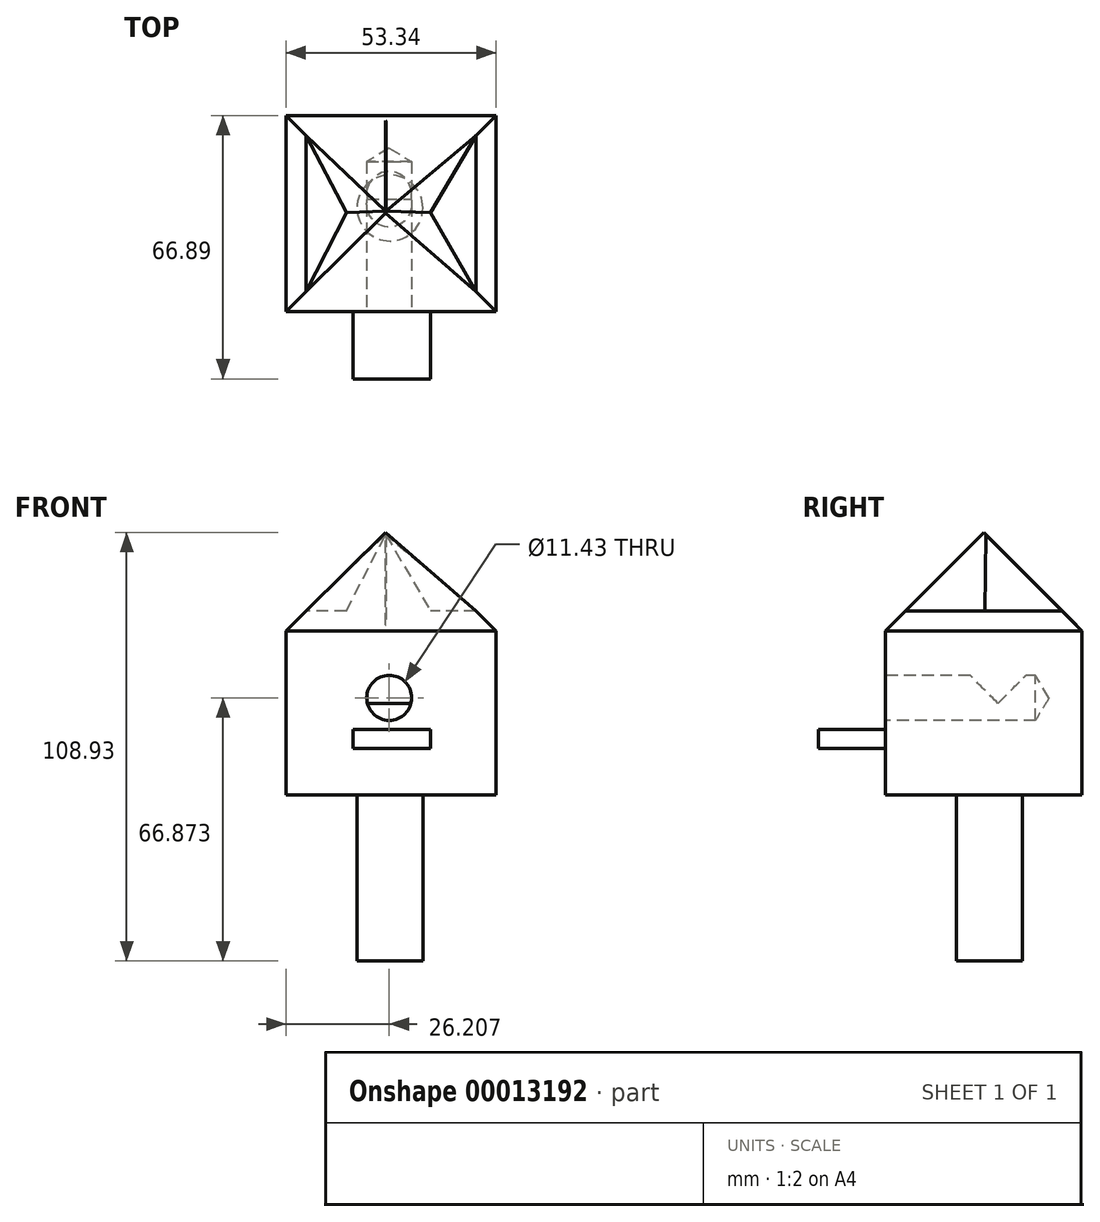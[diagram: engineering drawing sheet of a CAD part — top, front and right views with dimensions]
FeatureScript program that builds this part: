
annotation { "Feature Type Name" : "Feature", "Feature Type Description" : "" }
export const myFeature = defineFeature(function(context is Context, id is Id, definition is map)
    precondition{}
    {
        {
            var Q0;
            Q0=qCreatedBy(makeId("Front.planeOp"),FACE);
            var sketch = newSketch(context, id + "F0", { "sketchPlane" : qUnion([Q0])});
            skLineSegment(sketch, "E0.bottom", {"start": v(-41.12, 12.66) * mm, "end": v(12.22, 12.66) * mm});
            skLineSegment(sketch, "E0.top", {"start": v(-41.12, -34.12) * mm, "end": v(12.22, -34.12) * mm});
            skLineSegment(sketch, "E0.left", {"start": v(-41.12, 12.66) * mm, "end": v(-41.12, -34.12) * mm});
            skLineSegment(sketch, "E0.right", {"start": v(12.22, 12.66) * mm, "end": v(12.22, -34.12) * mm});
            skSolve(sketch);
        }
        {
            var Q0;
            Q0=makeQuery(id+"F0.imprint","IMPRINT",FACE,{"disambiguationData":[TD([[makeQuery(id+"F0.imprint","IMPRINT",EDGE,{"derivedFrom":sQuery(id+"F0.wireOp",EDGE,"E0.bottom")}),-1.0]])]});
            extrude(context, id + "F1", {"entities" : qUnion([Q0]), "oppositeDirection" : true, "depth" : 49.84 * mm});
        }
        {
            var Q0;
            Q0=makeQuery(id+"F1.opExtrude","SWEPT_FACE",FACE,{"disambiguationData":[OSD([sQuery(id+"F0.wireOp",EDGE,"E0.top")])]});
            var sketch = newSketch(context, id + "F2", { "sketchPlane" : qUnion([Q0])});
            skPoint(sketch, "E1", {"position": v(-14.75, -27.27) * mm});
            skSolve(sketch);
        }
        {
            var Q0;
            {var subQ0=sQuery(id+"F0.wireOp",EDGE,"E0.top");Q0=makeQuery(id+"F2.imprint","IMPRINT",FACE,{"disambiguationData":[TD([[makeQuery(id+"F2.imprint","IMPRINT",EDGE,{"derivedFrom":makeQuery(id+"F1.opExtrude","CAP_EDGE",EDGE,{"disambiguationData":[OSD([subQ0])],"isStart":true})}),-1.0]])]});}
            var sketch = newSketch(context, id + "F3", { "sketchPlane" : qUnion([Q0])});
            skCircle(sketch, "E2", {"center": v(-14.75, -26.37) * mm, "radius": 8.4 * mm});
            skSolve(sketch);
        }
        {
            var Q0;
            Q0=makeQuery(id+"F3.imprint","IMPRINT",FACE,{"disambiguationData":[TD([[makeQuery(id+"F3.imprint","IMPRINT",EDGE,{"derivedFrom":sQuery(id+"F3.wireOp",EDGE,"E2")}),1.0]])]});
            extrude(context, id + "F4", {"entities" : qUnion([Q0]), "operationType" : NewBodyOperationType.ADD, "depth" : 42.22 * mm});
        }
        {
            var Q0;
            Q0=makeQuery(id+"F1.opExtrude","CAP_FACE",FACE,{"disambiguationData":[OSD([sQuery(id+"F0.wireOp",EDGE,"E0.bottom"),sQuery(id+"F0.wireOp",EDGE,"E0.top"),sQuery(id+"F0.wireOp",EDGE,"E0.left"),sQuery(id+"F0.wireOp",EDGE,"E0.right")])],"isStart":true});
            var sketch = newSketch(context, id + "F5", { "sketchPlane" : qUnion([Q0])});
            skPoint(sketch, "E3", {"position": v(-14.91, -9.47) * mm});
            skSolve(sketch);
        }
        {
            var Q0;
            Q0=sQuery(id+"F5.wireOp",VERTEX,"E3");
            var Q1;
            Q1=makeQuery(id+"F1.opExtrude","SWEPT_BODY",BODY,{"disambiguationData":[OSD([sQuery(id+"F0.wireOp",EDGE,"E0.bottom"),sQuery(id+"F0.wireOp",EDGE,"E0.top"),sQuery(id+"F0.wireOp",EDGE,"E0.left"),sQuery(id+"F0.wireOp",EDGE,"E0.right")])]});
            hole(context, id + "F6", {"style" : HoleStyle.SIMPLE, "holeDiameter" : 11.43 * mm, "endStyle" : HoleEndStyle.BLIND, "holeDepth" : 38.1 * mm, "locations" : qUnion([Q0]), "scope" : qUnion([Q1])});
        }
        {
            var Q0;
            Q0=makeQuery(id+"F1.opExtrude","SWEPT_FACE",FACE,{"disambiguationData":[OSD([sQuery(id+"F0.wireOp",EDGE,"E0.bottom")])]});
            chamfer(context, id + "F7", {"entities" : qUnion([Q0]), "width" : 5.08 * mm, "tangentPropagation" : true});
        }
        {
            var Q0;
            {var subQ0=sQuery(id+"F0.wireOp",EDGE,"E0.bottom");Q0=makeQuery(id+"F7.opChamfer","BLEND_FACE",FACE,{"disambiguationData":[OSD([subQ0]),TDD([makeQuery(id+"F1.opExtrude","CAP_EDGE",EDGE,{"disambiguationData":[OSD([subQ0])],"isStart":true})])]});}
            var sketch = newSketch(context, id + "F8", { "sketchPlane" : qUnion([Q0])});
            skLineSegment(sketch, "E4", {"start": v(-36.04, 12.55) * mm, "end": v(-15.8, 40.72) * mm});
            skLineSegment(sketch, "E5", {"start": v(-15.8, 40.72) * mm, "end": v(7.14, 12.55) * mm});
            skSolve(sketch);
        }
        {
            var Q0;
            Q0=makeQuery(id+"F8.imprint","IMPRINT",FACE,{"disambiguationData":[TD([[makeQuery(id+"F8.imprint","IMPRINT",EDGE,{"derivedFrom":sQuery(id+"F8.wireOp",EDGE,"E4")}),-1.0]])]});
            extrude(context, id + "F9", {"entities" : qUnion([Q0]), "oppositeDirection" : true, "depth" : 33.23 * mm});
        }
        {
            var Q0;
            Q0=makeQuery(id+"F1.opExtrude","CAP_FACE",FACE,{"disambiguationData":[OSD([sQuery(id+"F0.wireOp",EDGE,"E0.bottom"),sQuery(id+"F0.wireOp",EDGE,"E0.top"),sQuery(id+"F0.wireOp",EDGE,"E0.left"),sQuery(id+"F0.wireOp",EDGE,"E0.right")])],"isStart":true});
            var sketch = newSketch(context, id + "F10", { "sketchPlane" : qUnion([Q0])});
            skLineSegment(sketch, "E6.bottom", {"start": v(-24.16, -17.52) * mm, "end": v(-4.47, -17.52) * mm});
            skLineSegment(sketch, "E6.top", {"start": v(-24.16, -22.3) * mm, "end": v(-4.47, -22.3) * mm});
            skLineSegment(sketch, "E6.left", {"start": v(-24.16, -17.52) * mm, "end": v(-24.16, -22.3) * mm});
            skLineSegment(sketch, "E6.right", {"start": v(-4.47, -17.52) * mm, "end": v(-4.47, -22.3) * mm});
            skSolve(sketch);
        }
        {
            var Q0;
            Q0=makeQuery(id+"F10.imprint","IMPRINT",FACE,{"disambiguationData":[TD([[makeQuery(id+"F10.imprint","IMPRINT",EDGE,{"derivedFrom":sQuery(id+"F10.wireOp",EDGE,"E6.bottom")}),-1.0]])]});
            extrude(context, id + "F11", {"entities" : qUnion([Q0]), "operationType" : NewBodyOperationType.ADD, "depth" : 17.05 * mm});
        }
        {
            var Q0;
            {var subQ0=sQuery(id+"F0.wireOp",EDGE,"E0.bottom");Q0=makeQuery(id+"F7.opChamfer","BLEND_FACE",FACE,{"disambiguationData":[OSD([subQ0]),TDD([makeQuery(id+"F1.opExtrude","CAP_EDGE",EDGE,{"disambiguationData":[OSD([subQ0])],"isStart":false})])]});}
            var sketch = newSketch(context, id + "F12", { "sketchPlane" : qUnion([Q0])});
            skLineSegment(sketch, "E7", {"start": v(-7.14, -22.7) * mm, "end": v(15.8, 4.64) * mm});
            skLineSegment(sketch, "E8", {"start": v(15.8, 4.64) * mm, "end": v(36.04, -22.7) * mm});
            skSolve(sketch);
        }
        {
            var Q0;
            Q0=makeQuery(id+"F12.imprint","IMPRINT",FACE,{"disambiguationData":[TD([[makeQuery(id+"F12.imprint","IMPRINT",EDGE,{"derivedFrom":sQuery(id+"F12.wireOp",EDGE,"E7")}),-1.0]])]});
            extrude(context, id + "F13", {"entities" : qUnion([Q0]), "operationType" : NewBodyOperationType.ADD, "oppositeDirection" : true, "depth" : 25.64 * mm});
        }
    });
